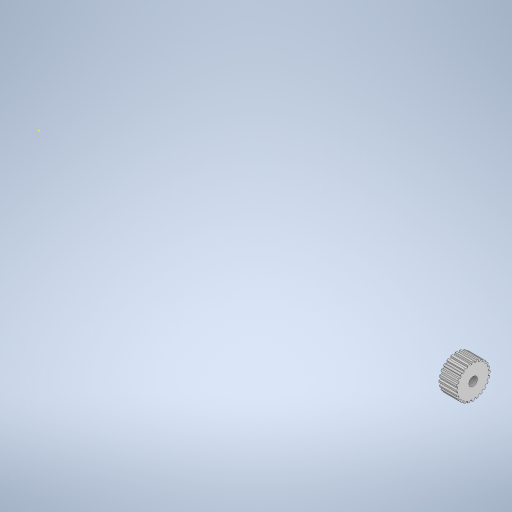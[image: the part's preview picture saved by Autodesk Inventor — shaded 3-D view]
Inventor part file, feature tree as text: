
AUTODESK INVENTOR PART (.ipt)
format: ipt  version: 2024 (Build 280153000, 153)  size: 368,640 bytes
history: native  units: in
note: dims shown in document units (in); Inventor stores cm internally (conversion verified against a paired STEP export)
features: plane x3, sketch x3, extrude x2
ambient origin geometry x8: Origin, YZ Plane, XZ Plane, XY Plane, X Axis, Y Axis, Z Axis, Center Point
bodies: Solid1 (feature_tree)
feature tree (8):
  plane  "Work Plane1"
  plane  "Work Plane2"
  extrude  "Extrusion3"  Depth=0.0394in
  plane  "Work Plane3"
  extrude  "Extrusion4"  Depth=0.3937in TaperAngle=0.0deg
  sketch  "Sketch5"  dims[d32=0.1969in d33=0.3937in d34=0.0in]
  sketch  "Sketch3"  dims[d24=0.0591in d25=0.0394in]
  sketch  "Sketch4"  dims[d26=9.4488in d28=360.0deg d30=0.3937in d31=0.0in]
